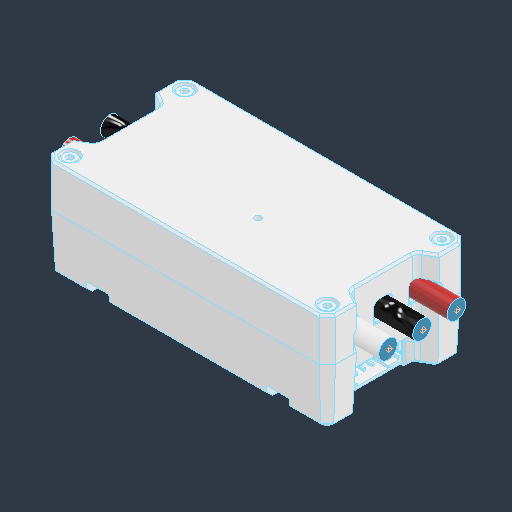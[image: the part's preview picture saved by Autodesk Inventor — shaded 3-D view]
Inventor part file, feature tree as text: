
AUTODESK INVENTOR PART (.ipt)
format: ipt  version: 2024.3 (Build 283343000, 343)  size: 2,232,832 bytes
history: native  units: in
note: dims shown in document units (in); Inventor stores cm internally (conversion verified against a paired STEP export)
features: other x18, sketch x4
ambient origin geometry x8: Origin, YZ Plane, XZ Plane, XY Plane, X Axis, Y Axis, Z Axis, Center Point
bodies: Solid1 (feature_tree), Solid2 (feature_tree), Solid3 (feature_tree), Solid4 (feature_tree), Solid5 (feature_tree), Solid6 (feature_tree), Solid7 (feature_tree), Solid8 (feature_tree), Solid9 (feature_tree), Solid10 (feature_tree), Solid11 (feature_tree), Solid12 (feature_tree), Solid13 (feature_tree), Solid14 (feature_tree), Solid15 (feature_tree), Solid16 (feature_tree), Solid17 (feature_tree), Solid18 (feature_tree)
feature tree (22):
  sketch  "Sketch1"
  sketch  "Sketch2"
  sketch  "Sketch3"
  sketch  "Sketch4"
  parser-record x1  (decoder bookkeeping rows leaked as tree rows — omitted from the tree; the rows remain in map.json)
  other  "NONE:1"
  other  "NONE:2"
  other  "NONE:3"
  other  "NONE:4"
  other  "NONE:5"
  other  "NONE:6"
  other  "NONE:7"
  other  "NONE:8"
  other  "NONE:9"
  other  "NONE:10"
  other  "NONE:11"
  other  "NONE:12"
  other  "Cut-Extrude1[1]"
  other  "Cut-Extrude1[2]"
  other  "Cut-Extrude1[3]"
  other  "Cut-Extrude1[4]"
  other  "Cut-Extrude1[5]"
